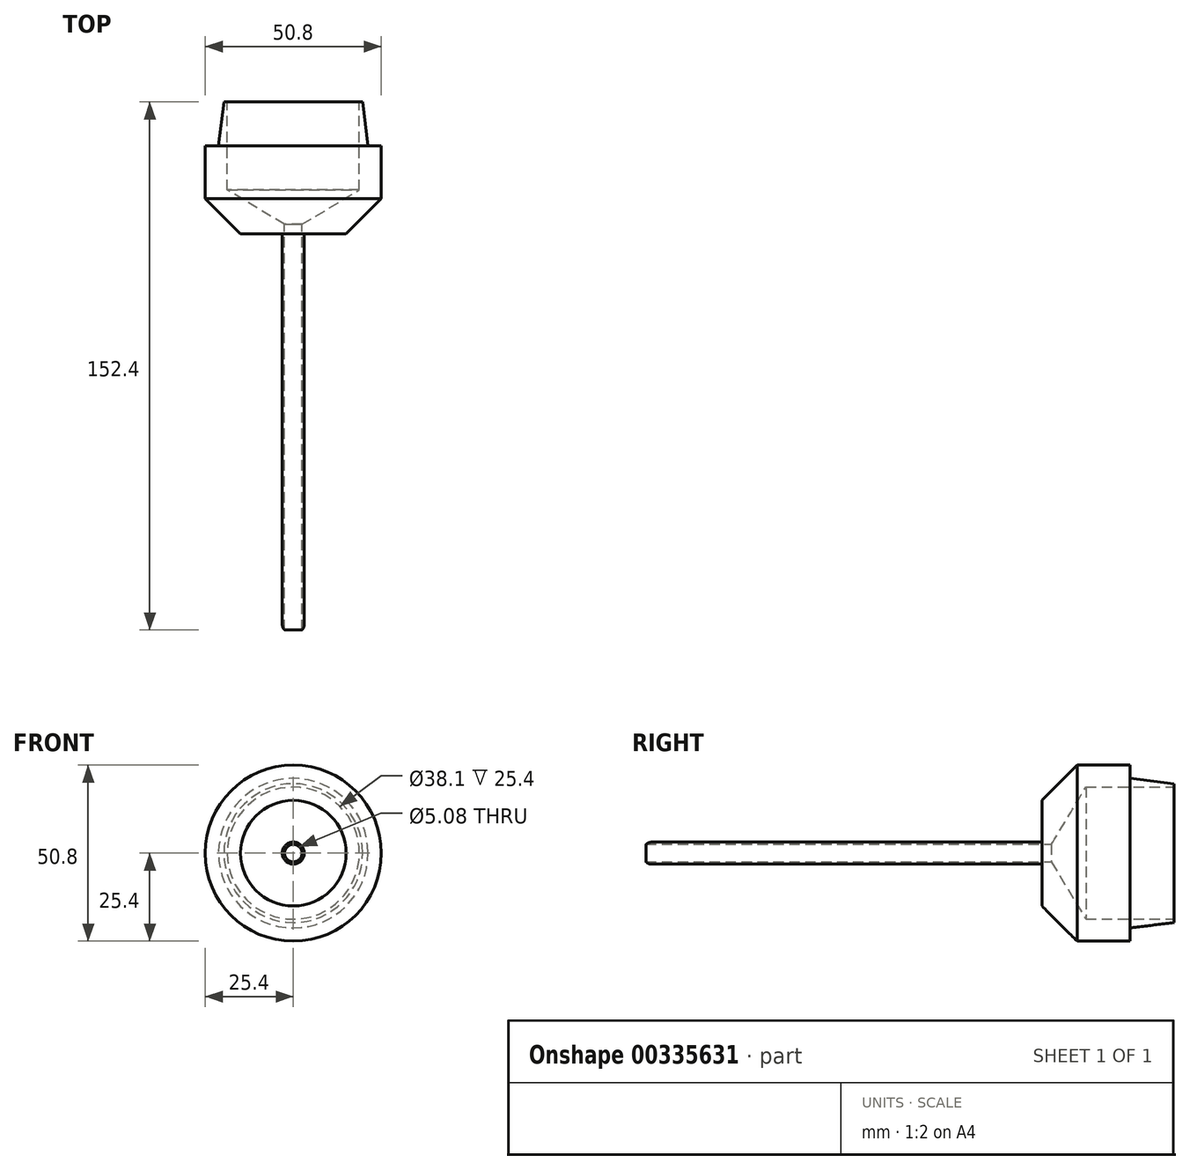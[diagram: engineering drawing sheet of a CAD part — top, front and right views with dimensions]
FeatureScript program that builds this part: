
annotation { "Feature Type Name" : "Feature", "Feature Type Description" : "" }
export const myFeature = defineFeature(function(context is Context, id is Id, definition is map)
    precondition{}
    {
        {
            var Q0;
            Q0=qCreatedBy(makeId("Front.planeOp"),FACE);
            var sketch = newSketch(context, id + "F0", { "sketchPlane" : qUnion([Q0])});
            skCircle(sketch, "E0", {"center": v(0, 0) * mm, "radius": 21.59 * mm});
            skSolve(sketch);
        }
        {
            var Q0;
            Q0=qSketchRegion(id+"F0",true);
            extrude(context, id + "F1", {"entities" : qUnion([Q0]), "depth" : 12.7 * mm});
        }
        {
            var Q0;
            Q0=makeQuery(id+"F1.opExtrude","CAP_FACE",FACE,{"disambiguationData":[OSD([sQuery(id+"F0.wireOp",EDGE,"E0")])],"isStart":false});
            var sketch = newSketch(context, id + "F2", { "sketchPlane" : qUnion([Q0])});
            skCircle(sketch, "E1", {"center": v(0, 0) * mm, "radius": 25.4 * mm});
            skSolve(sketch);
        }
        {
            var Q0;
            Q0=qSketchRegion(id+"F2",true);
            extrude(context, id + "F3", {"entities" : qUnion([Q0]), "operationType" : NewBodyOperationType.ADD, "depth" : 25.4 * mm});
        }
        {
            var Q0;
            Q0=makeQuery(id+"F3.opExtrude","CAP_EDGE",EDGE,{"disambiguationData":[OSD([sQuery(id+"F2.wireOp",EDGE,"E1")])],"isStart":false});
            chamfer(context, id + "F4", {"entities" : qUnion([Q0]), "width" : 10.16 * mm, "tangentPropagation" : true});
        }
        {
            var Q0;
            Q0=makeQuery(id+"F3.opExtrude","CAP_FACE",FACE,{"disambiguationData":[OSD([sQuery(id+"F2.wireOp",EDGE,"E1")])],"isStart":false});
            var sketch = newSketch(context, id + "F5", { "sketchPlane" : qUnion([Q0])});
            skLineSegment(sketch, "E2.bottom", {"start": v(3.17, -3.18) * mm, "end": v(-3.18, -3.18) * mm});
            skLineSegment(sketch, "E2.top", {"start": v(3.17, 3.18) * mm, "end": v(-3.18, 3.18) * mm});
            skLineSegment(sketch, "E2.left", {"start": v(3.17, -3.18) * mm, "end": v(3.18, 3.18) * mm});
            skLineSegment(sketch, "E2.right", {"start": v(-3.18, -3.18) * mm, "end": v(-3.18, 3.17) * mm});
            skPoint(sketch, "E2.middle", {"position": v(0, 0) * mm});
            skSolve(sketch);
        }
        {
            var Q0;
            Q0=qSketchRegion(id+"F5",true);
            extrude(context, id + "F6", {"entities" : qUnion([Q0]), "operationType" : NewBodyOperationType.ADD, "depth" : 114.3 * mm});
        }
        {
            var Q0;
            Q0=makeQuery(id+"F6.opExtrude","SWEPT_EDGE",EDGE,{"disambiguationData":[OSD([sQuery(id+"F5.wireOp",EDGE,"E2.bottom"),sQuery(id+"F5.wireOp",EDGE,"E2.left")])]});
            var Q1;
            Q1=makeQuery(id+"F6.opExtrude","SWEPT_EDGE",EDGE,{"disambiguationData":[OSD([sQuery(id+"F5.wireOp",EDGE,"E2.top"),sQuery(id+"F5.wireOp",EDGE,"E2.left")])]});
            var Q2;
            Q2=makeQuery(id+"F6.opExtrude","SWEPT_EDGE",EDGE,{"disambiguationData":[OSD([sQuery(id+"F5.wireOp",EDGE,"E2.top"),sQuery(id+"F5.wireOp",EDGE,"E2.right")])]});
            var Q3;
            Q3=makeQuery(id+"F6.opExtrude","SWEPT_EDGE",EDGE,{"disambiguationData":[OSD([sQuery(id+"F5.wireOp",EDGE,"E2.bottom"),sQuery(id+"F5.wireOp",EDGE,"E2.right")])]});
            fillet(context, id + "F7", {"entities" : qUnion([Q0, Q1, Q2, Q3]), "radius" : 3.17 * mm, "tangentPropagation" : true, "allowEdgeOverflow" : false});
        }
        {
            var Q0;
            Q0=makeQuery(id+"F1.opExtrude","CAP_FACE",FACE,{"disambiguationData":[OSD([sQuery(id+"F0.wireOp",EDGE,"E0")])],"isStart":true});
            var sketch = newSketch(context, id + "F8", { "sketchPlane" : qUnion([Q0])});
            skCircle(sketch, "E3", {"center": v(0, 0) * mm, "radius": 19.05 * mm});
            skSolve(sketch);
        }
        {
            var Q0;
            Q0=sQuery(id+"F8.wireOp",VERTEX,"E3.center");
            var Q1;
            Q1=makeQuery(id+"F1.opExtrude","SWEPT_BODY",BODY,{"disambiguationData":[OSD([sQuery(id+"F0.wireOp",EDGE,"E0")])]});
            hole(context, id + "F9", {"style" : HoleStyle.SIMPLE, "endStyle" : HoleEndStyle.BLIND, "holeDiameter" : 38.1 * mm, "holeDepth" : 25.4 * mm, "tappedDepth" : 12.7 * mm, "tapClearance" : 3, "locations" : qUnion([Q0]), "scope" : qUnion([Q1])});
        }
        {
            var Q0;
            Q0=qCreatedBy(makeId("Front.planeOp"),FACE);
            var sketch = newSketch(context, id + "F10", { "sketchPlane" : qUnion([Q0])});
            skCircle(sketch, "E4", {"center": v(0, 0) * mm, "radius": 1.46 * mm});
            skSolve(sketch);
        }
        {
            var Q0;
            Q0=sQuery(id+"F10.wireOp",VERTEX,"E4.center");
            var Q1;
            Q1=makeQuery(id+"F1.opExtrude","SWEPT_BODY",BODY,{"disambiguationData":[OSD([sQuery(id+"F0.wireOp",EDGE,"E0")])]});
            hole(context, id + "F11", {"style" : HoleStyle.SIMPLE, "endStyle" : HoleEndStyle.BLIND, "oppositeDirection" : true, "holeDiameter" : 5.08 * mm, "holeDepth" : 254 * mm, "tappedDepth" : 12.7 * mm, "tapClearance" : 3, "locations" : qUnion([Q0]), "scope" : qUnion([Q1])});
        }
        {
            var Q0;
            Q0=makeQuery(id+"F1.opExtrude","CAP_EDGE",EDGE,{"disambiguationData":[OSD([sQuery(id+"F0.wireOp",EDGE,"E0")])],"isStart":true});
            chamfer(context, id + "F12", {"entities" : qUnion([Q0]), "chamferType" : ChamferType.OFFSET_ANGLE, "width" : 12.7 * mm, "oppositeDirection" : false, "angle" : 7 * degree, "tangentPropagation" : true});
        }
        {
            var Q0;
            {var subQ0=sQuery(id+"F5.wireOp",EDGE,"E2.left");var subQ1=sQuery(id+"F5.wireOp",EDGE,"E2.bottom");Q0=makeQuery(id+"F7.opFillet","BLEND_EDGE",EDGE,{"blendedFrom":[makeQuery(id+"F6.opExtrude","SWEPT_EDGE",EDGE,{"disambiguationData":[OSD([subQ1,subQ0])]}),makeQuery(id+"F6.opExtrude","CAP_FACE",FACE,{"disambiguationData":[OSD([subQ1,sQuery(id+"F5.wireOp",EDGE,"E2.top"),subQ0,sQuery(id+"F5.wireOp",EDGE,"E2.right")])],"isStart":false})],"blendedInto":[makeQuery(id+"F6.opExtrude","CAP_FACE",FACE,{"disambiguationData":[OSD([subQ1,sQuery(id+"F5.wireOp",EDGE,"E2.top"),subQ0,sQuery(id+"F5.wireOp",EDGE,"E2.right")])],"isStart":false})]});}
            fillet(context, id + "F13", {"entities" : qUnion([Q0]), "radius" : 2.54 * mm, "tangentPropagation" : true, "allowEdgeOverflow" : false});
        }
    });
